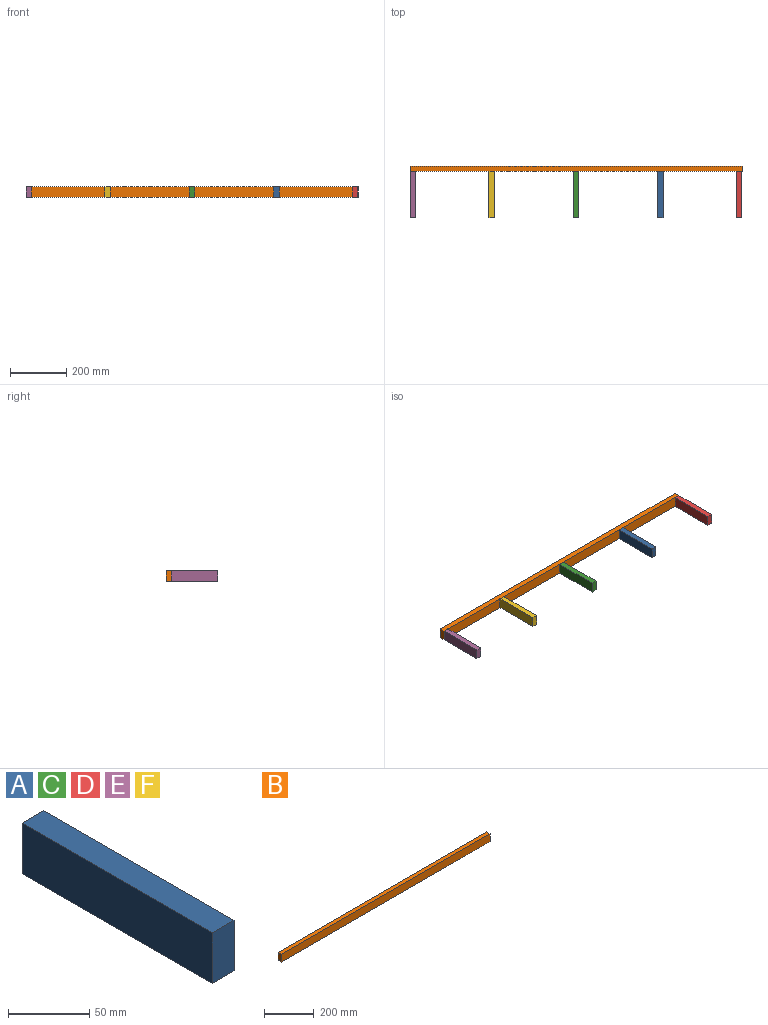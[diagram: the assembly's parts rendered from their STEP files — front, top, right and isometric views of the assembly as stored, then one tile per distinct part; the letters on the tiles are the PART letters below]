
ASSEMBLY  parts=6 mates=5
PART A: 6 faces, bbox 19.1x165.1x38.1 mm
  f0: plane 38.1x19.05mm, normal (0,1,0), area 725.8mm2, adj f1,f3,f4,f5
  f1: plane 165.1x19.05mm, normal (0,0,1), area 3145.2mm2, adj f0,f2,f4,f5
  f2: plane 38.1x19.05mm, normal (0,-1,0), area 725.8mm2, adj f1,f3,f4,f5
  f3: plane 165.1x19.05mm, normal (0,0,-1), area 3145.2mm2, adj f0,f2,f4,f5
  f4: plane 165.1x38.1mm, normal (1,0,0), area 6290.3mm2, adj f0,f1,f2,f3
  f5: plane 165.1x38.1mm, normal (-1,0,0), area 6290.3mm2, adj f0,f1,f2,f3
PART B: 6 faces, bbox 1181.1x19.1x38.1 mm
  f0: plane 1181.1x19.05mm, normal (0,0,1), area 22500mm2, adj f1,f3,f4,f5
  f1: plane 38.1x19.05mm, normal (-1,0,0), area 725.8mm2, adj f0,f2,f4,f5
  f2: plane 1181.1x19.05mm, normal (0,0,-1), area 22500mm2, adj f1,f3,f4,f5
  f3: plane 38.1x19.05mm, normal (1,0,0), area 725.8mm2, adj f0,f2,f4,f5
  f4: plane 1181.1x38.1mm, normal (0,-1,0), area 44999.9mm2, adj f0,f1,f2,f3
  f5: plane 1181.1x38.1mm, normal (0,1,0), area 44999.9mm2, adj f0,f1,f2,f3
PART C: same geometry as A
PART D: same geometry as A
PART E: same geometry as A
PART F: same geometry as A
PLACE A t=(881.06,-19.05,0)mm
PLACE B at identity fixed
PLACE C t=(581.03,-19.05,0)mm
PLACE D t=(1162.05,-19.05,0)mm
PLACE E t=(0,-19.05,0)mm
PLACE F t=(280.99,-19.05,0)mm
MATE fastened C.f0 <-> B.f4  axis (0,1,0) through (590.55,-19.05,19.05)mm
MATE fastened D.f4 <-> B.f3  axis (1,0,0) through (1181.1,-19.05,19.05)mm
MATE fastened B.f4 <-> F.f0  axis (0,-1,0) through (290.51,-19.05,19.05)mm
MATE fastened B.f4 <-> A.f0  axis (0,-1,0) through (890.59,-19.05,19.05)mm
MATE fastened B.f1 <-> E.f5  axis (-1,0,0) through (0,-19.05,19.05)mm
